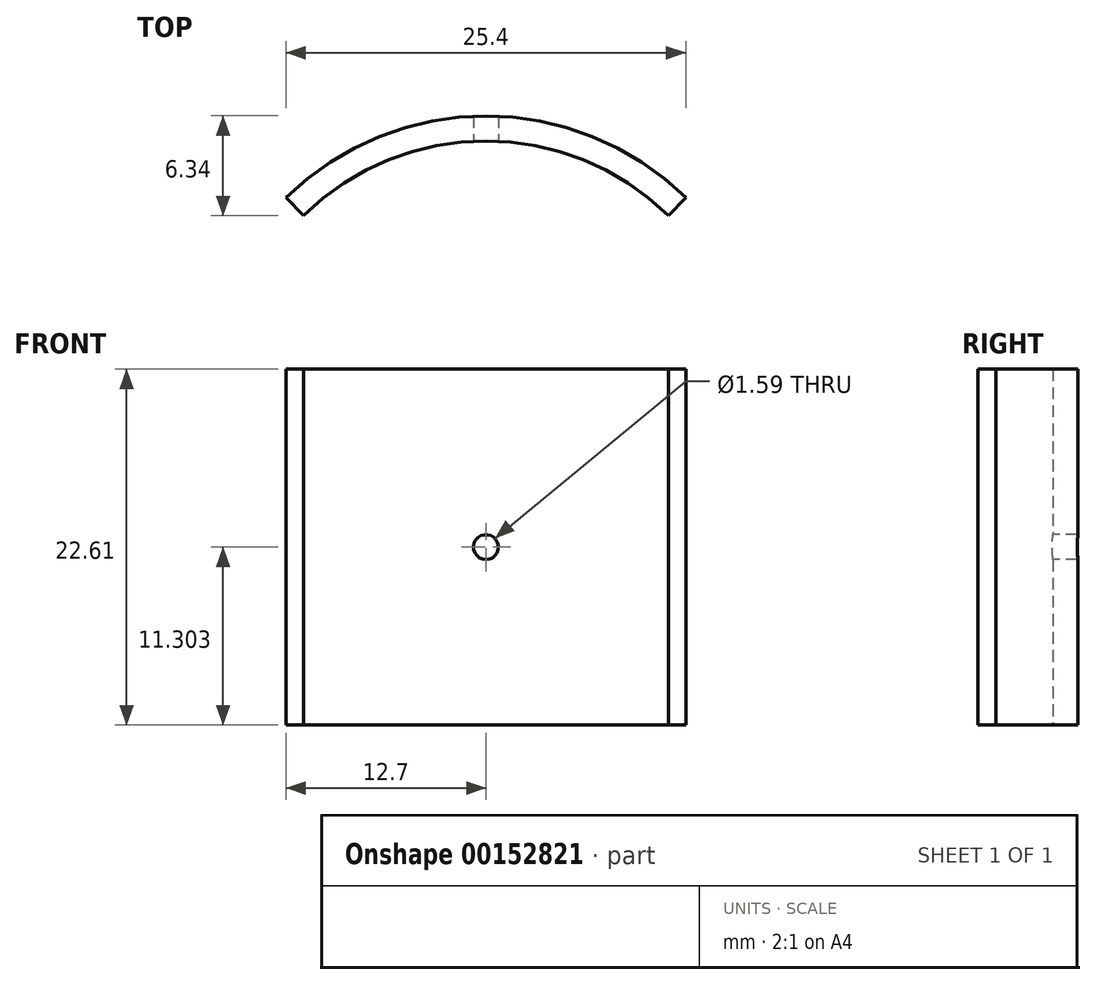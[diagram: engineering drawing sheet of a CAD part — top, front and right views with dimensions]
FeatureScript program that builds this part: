
annotation { "Feature Type Name" : "Feature", "Feature Type Description" : "" }
export const myFeature = defineFeature(function(context is Context, id is Id, definition is map)
    precondition{}
    {
        {
            var Q0;
            Q0=qCreatedBy(makeId("Top.planeOp"),FACE);
            var sketch = newSketch(context, id + "F0", { "sketchPlane" : qUnion([Q0])});
            skArc(sketch, "E0", {"start": v(11.59, 11.76) * mm, "mid": v(0, 16.51) * mm, "end": v(-11.59, 11.76) * mm});
            skLineSegment(sketch, "E1", {"start": v(0, 0) * mm, "end": v(11.59, 11.76) * mm, "construction": true});
            skLineSegment(sketch, "E2", {"start": v(0, 0) * mm, "end": v(-11.59, 11.76) * mm, "construction": true});
            skLineSegment(sketch, "E3", {"start": v(0, 0) * mm, "end": v(0, 16.51) * mm, "construction": true});
            skLineSegment(sketch, "E4", {"start": v(11.59, 11.76) * mm, "end": v(12.7, 12.9) * mm});
            skLineSegment(sketch, "E5", {"start": v(-11.59, 11.76) * mm, "end": v(-12.7, 12.9) * mm});
            skArc(sketch, "E6", {"start": v(12.7, 12.9) * mm, "mid": v(0, 18.1) * mm, "end": v(-12.7, 12.9) * mm});
            skSolve(sketch);
        }
        {
            var Q0;
            Q0=qSketchRegion(id+"F0",true);
            extrude(context, id + "F1", {"entities" : qUnion([Q0]), "depth" : 22.6 * mm});
        }
        {
            var Q0;
            Q0=qCreatedBy(makeId("Front.planeOp"),FACE);
            var sketch = newSketch(context, id + "F2", { "sketchPlane" : qUnion([Q0])});
            skLineSegment(sketch, "E7", {"start": v(0, 0) * mm, "end": v(0, 22.6) * mm, "construction": true});
            skCircle(sketch, "E8", {"center": v(0, 11.3) * mm, "radius": 0.8 * mm});
            skSolve(sketch);
        }
        {
            var Q0;
            Q0=qSketchRegion(id+"F2",true);
            var Q1;
            Q1=makeQuery(id+"F1.opExtrude","SWEPT_FACE",FACE,{"disambiguationData":[OSD([sQuery(id+"F0.wireOp",EDGE,"E6")])]});
            extrude(context, id + "F3", {"entities" : qUnion([Q0]), "operationType" : NewBodyOperationType.REMOVE, "endBound" : BoundingType.UP_TO_SURFACE, "oppositeDirection" : true, "endBoundEntityFace" : qUnion([Q1]), "depth" : 25.4 * mm});
        }
    });
